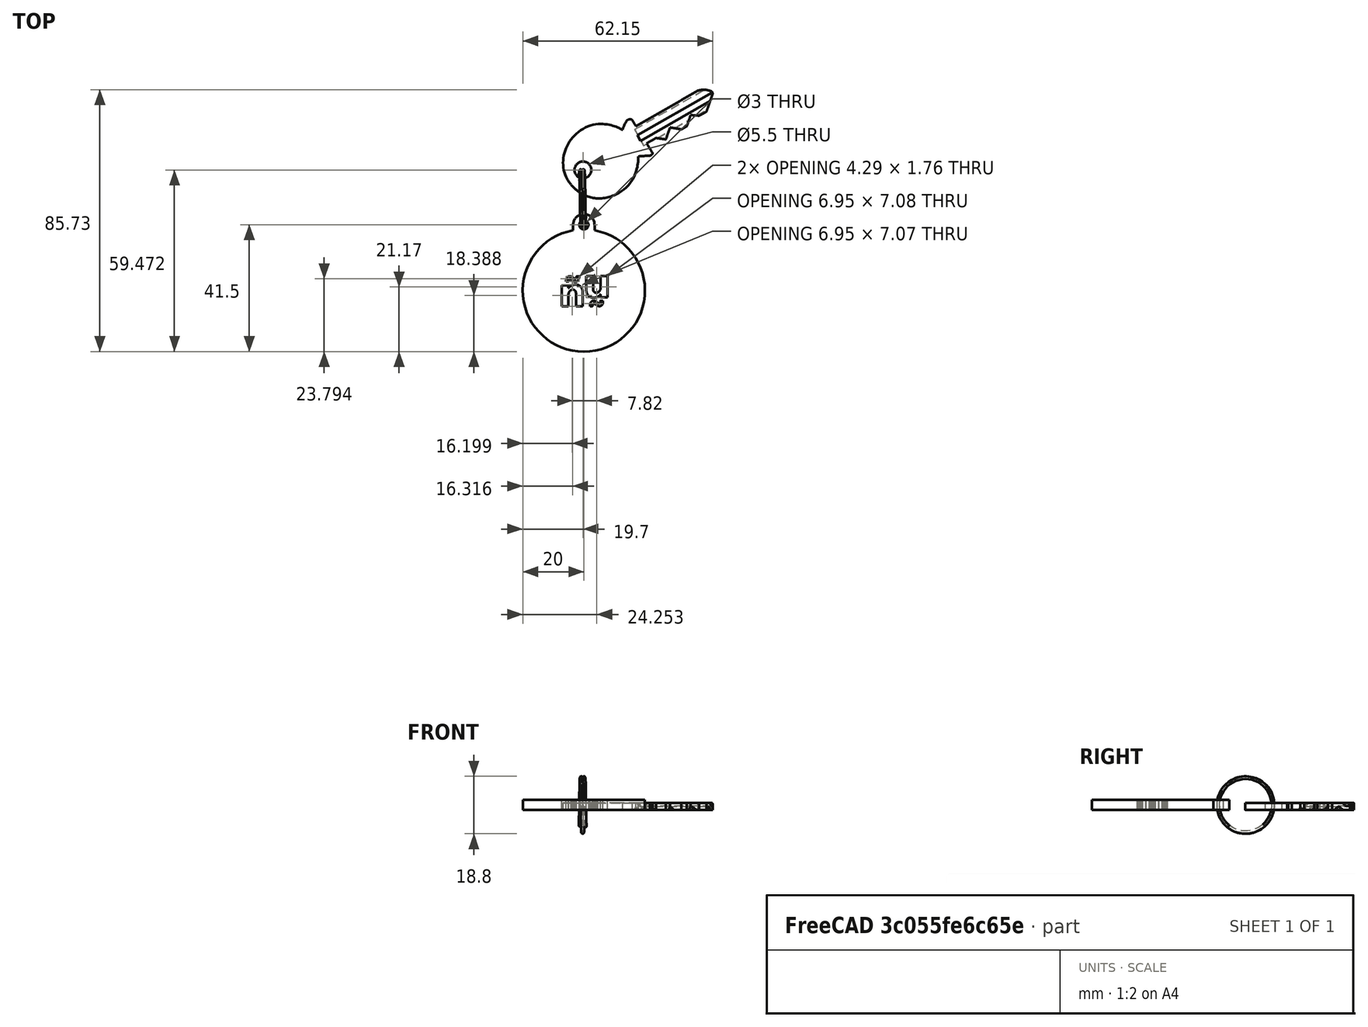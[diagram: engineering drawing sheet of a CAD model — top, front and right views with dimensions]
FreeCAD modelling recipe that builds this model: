
FCSTD DOCUMENT  (FreeCAD 0.18R16158 (Git))
Label: nu
License: CreativeCommons Attribution-ShareAlike
LicenseURL: http://creativecommons.org/licenses/by-sa/4.0/
objects: Part::Feature×6, Part::Extrusion×4, App::DocumentObjectGroup×2, Part::FeaturePython×1, Part::MultiFuse×1, Part::Cut×1
note: 13 computed .brp shape members not serialized (recipe doc carries the construction recipe); baked Part::Feature solids carry a one-line shape summary decoded from their .brp

FEATURE [App::DocumentObjectGroup] Group001  label="Casino-chip-src"
FEATURE [Part::Feature] Sweep  label="key-ring-model-1"
  Placement = pos=(-1.2,30.2546,1.6391) rot=(0.333333,0.881918,0.333333;1.69612rad)
  shape: bbox 3.31 x 27.02 x 26.33 mm, 4 faces (baked)
FEATURE [Part::Feature] Cut  label="key-model-1"
  Placement = pos=(-5.46976,36.5266,0) rot=(0,0,1;0.517888rad)
  shape: bbox 49.82 x 36.6 x 2.3 mm, 44 faces (baked)
FEATURE [App::DocumentObjectGroup] Group  label="Assembly"
  Group = -> [Sweep,Cut]
FEATURE [Part::FeaturePython] Clone  label="Clone-of-casino-chip"  # WARN: FeaturePython — macro-defined, semantics opaque (R4)
  Scale = (1,1,1)
FEATURE [Part::Feature] path837
  shape: bbox 6.945 x 7.075 x 3.173e-07 mm, 0 faces, 0 solids (baked)
FEATURE [Part::Feature] path837001
  shape: bbox 4.293 x 1.764 x 3.173e-07 mm, 0 faces, 0 solids (baked)
FEATURE [Part::Feature] path834
  shape: bbox 6.945 x 7.075 x 3.173e-07 mm, 0 faces, 0 solids (baked)
FEATURE [Part::Feature] path834001
  shape: bbox 4.293 x 1.764 x 3.173e-07 mm, 0 faces, 0 solids (baked)
FEATURE [Part::Extrusion] Extrude
  Base = -> path837
  Dir = (0,0,-1)
  DirMode = 2
  FaceMakerClass = Part::FaceMakerBullseye
  LengthFwd = 4
  LengthRev = 0
  Reversed = true
  Solid = true
  Symmetric = false
FEATURE [Part::Extrusion] Extrude001
  Base = -> path837001
  Dir = (0,0,-1)
  DirMode = 2
  FaceMakerClass = Part::FaceMakerBullseye
  LengthFwd = 4
  LengthRev = 0
  Reversed = true
  Solid = true
  Symmetric = false
FEATURE [Part::Extrusion] Extrude002
  Base = -> path834
  Dir = (0,0,-1)
  DirMode = 2
  FaceMakerClass = Part::FaceMakerBullseye
  LengthFwd = 4
  LengthRev = 0
  Reversed = true
  Solid = true
  Symmetric = false
FEATURE [Part::Extrusion] Extrude003
  Base = -> path834001
  Dir = (0,0,-1)
  DirMode = 2
  FaceMakerClass = Part::FaceMakerBullseye
  LengthFwd = 4
  LengthRev = 0
  Reversed = true
  Solid = true
  Symmetric = false
FEATURE [Part::MultiFuse] Fusion
  Shapes = -> [Extrude,Extrude001,Extrude002,Extrude003]
FEATURE [Part::Cut] Cut001
  Base = -> Clone
  Tool = -> Fusion
